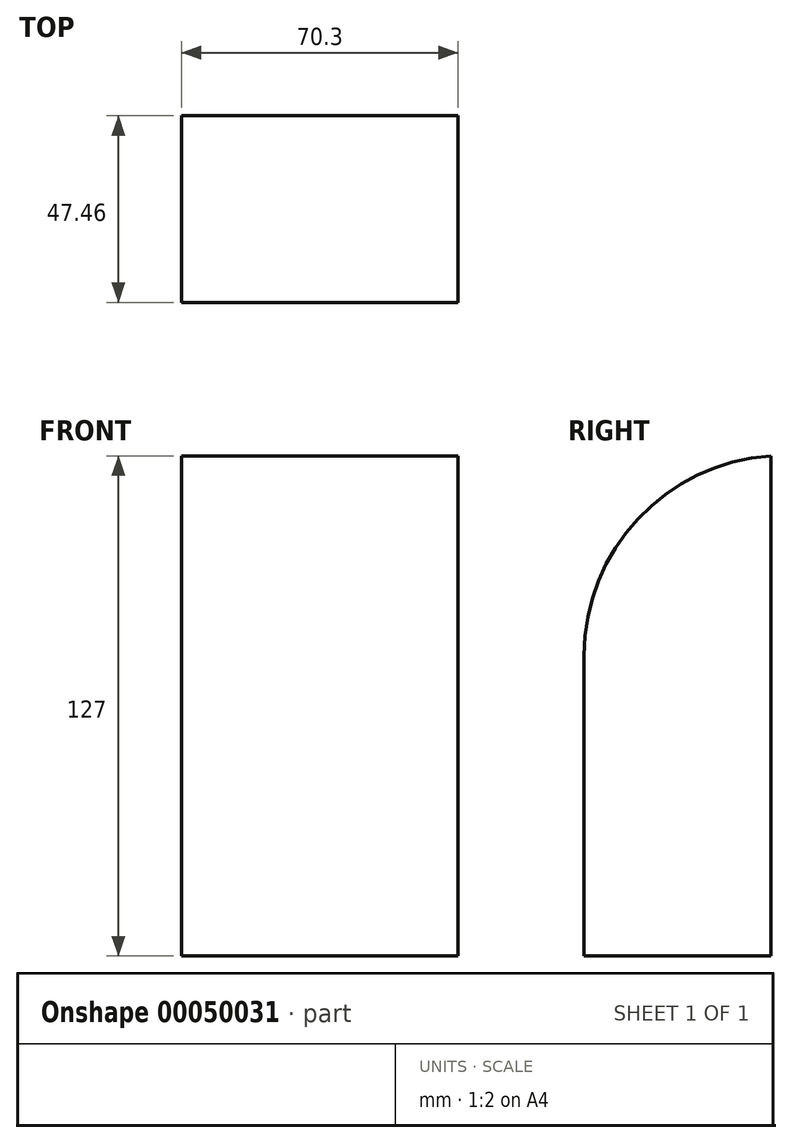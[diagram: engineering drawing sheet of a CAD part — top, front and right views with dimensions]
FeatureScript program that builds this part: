
annotation { "Feature Type Name" : "Feature", "Feature Type Description" : "" }
export const myFeature = defineFeature(function(context is Context, id is Id, definition is map)
    precondition{}
    {
        {
            var Q0;
            Q0=qCreatedBy(makeId("Top.planeOp"),FACE);
            var sketch = newSketch(context, id + "F1", { "sketchPlane" : qUnion([Q0])});
            skLineSegment(sketch, "E0.rect.bottom", {"start": v(35.15, -23.73) * mm, "end": v(-35.15, -23.73) * mm});
            skLineSegment(sketch, "E0.rect.top", {"start": v(35.15, 23.73) * mm, "end": v(-35.15, 23.73) * mm});
            skLineSegment(sketch, "E0.rect.left", {"start": v(35.15, -23.73) * mm, "end": v(35.15, 23.73) * mm});
            skLineSegment(sketch, "E0.rect.right", {"start": v(-35.15, -23.73) * mm, "end": v(-35.15, 23.73) * mm});
            skPoint(sketch, "E0.rect.middle", {"position": v(0, 0) * mm});
            skSolve(sketch);
        }
        {
            var Q0;
            Q0=makeQuery(id+"F1.imprint","IMPRINT",FACE,{"disambiguationData":[TD([[makeQuery(id+"F1.imprint","IMPRINT",EDGE,{"derivedFrom":sQuery(id+"F1.wireOp",EDGE,"E0.rect.bottom")}),-1.0]])]});
            extrude(context, id + "F0", {"entities" : qUnion([Q0]), "depth" : 127 * mm});
        }
        {
            var Q0;
            Q0=makeQuery(id+"F0.opExtrude","CAP_EDGE",EDGE,{"disambiguationData":[OSD([sQuery(id+"F1.wireOp",EDGE,"E0.rect.bottom")])],"isStart":false});
            fillet(context, id + "F2", {"entities" : qUnion([Q0]), "radius" : 50.8 * mm, "tangentPropagation" : true, "allowEdgeOverflow" : false});
        }
    });
